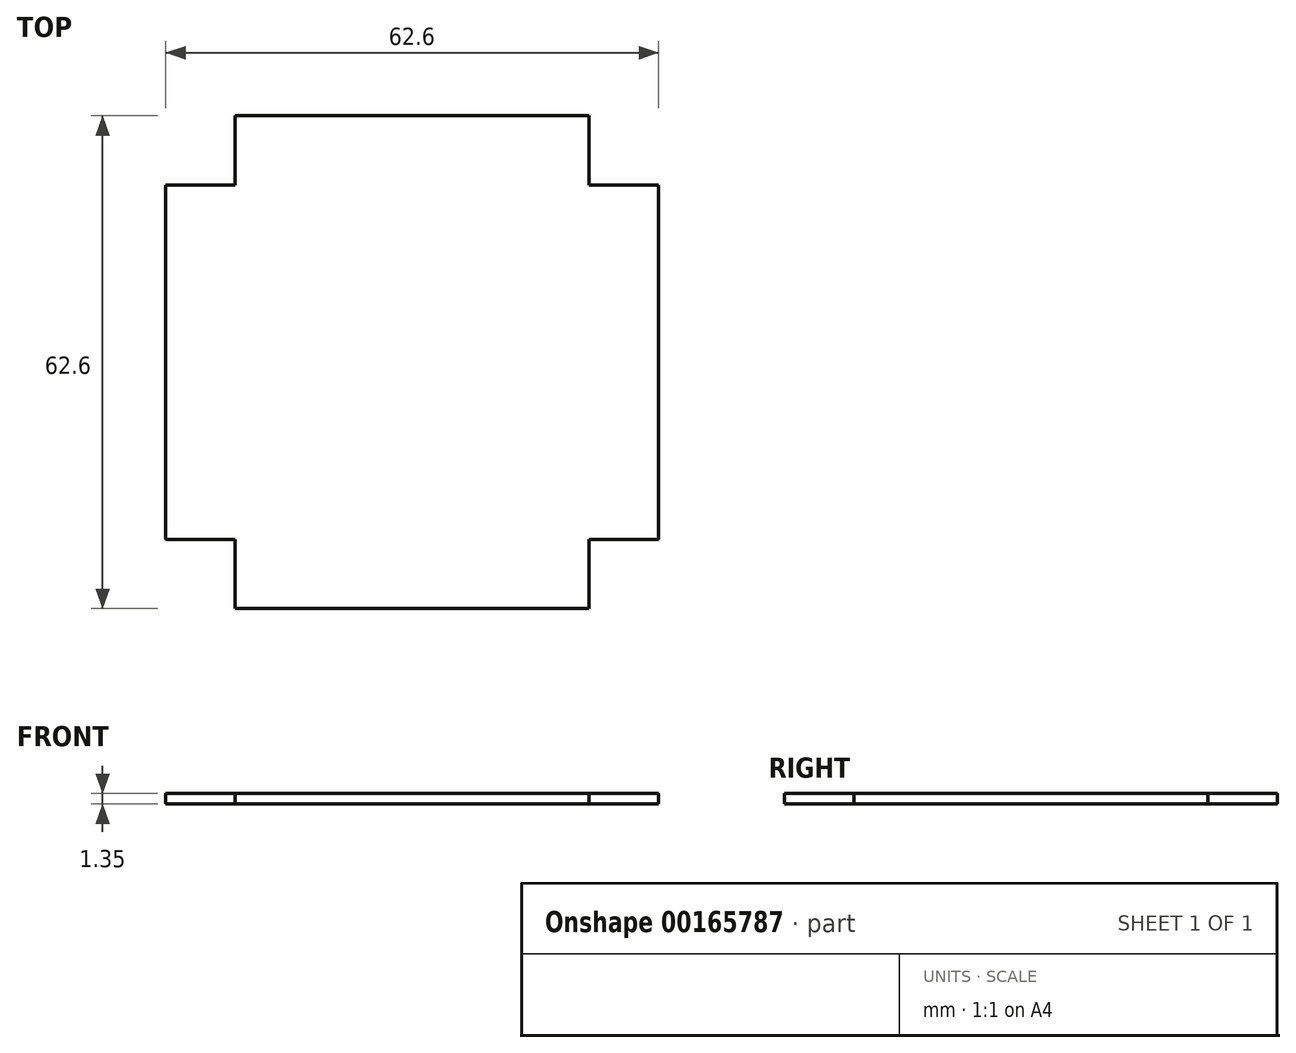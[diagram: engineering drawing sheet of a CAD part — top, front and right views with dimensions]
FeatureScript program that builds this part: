
annotation { "Feature Type Name" : "Feature", "Feature Type Description" : "" }
export const myFeature = defineFeature(function(context is Context, id is Id, definition is map)
    precondition{}
    {
        {
            var Q0;
            Q0=qCreatedBy(makeId("Top.planeOp"),FACE);
            var sketch = newSketch(context, id + "F0", { "sketchPlane" : qUnion([Q0])});
            skLineSegment(sketch, "E0.bottom", {"start": v(31.3, 22.5) * mm, "end": v(-31.3, 22.5) * mm});
            skLineSegment(sketch, "E0.top", {"start": v(31.3, -22.5) * mm, "end": v(-31.3, -22.5) * mm});
            skLineSegment(sketch, "E0.left", {"start": v(31.3, 22.5) * mm, "end": v(31.3, -22.5) * mm});
            skLineSegment(sketch, "E0.right", {"start": v(-31.3, 22.5) * mm, "end": v(-31.3, -22.5) * mm});
            skPoint(sketch, "E0.middle", {"position": v(0, 0) * mm});
            skLineSegment(sketch, "E1.bottom", {"start": v(22.5, 31.3) * mm, "end": v(-22.5, 31.3) * mm});
            skLineSegment(sketch, "E1.top", {"start": v(22.5, -31.3) * mm, "end": v(-22.5, -31.3) * mm});
            skLineSegment(sketch, "E1.left", {"start": v(22.5, 31.3) * mm, "end": v(22.5, -31.3) * mm});
            skLineSegment(sketch, "E1.right", {"start": v(-22.5, 31.3) * mm, "end": v(-22.5, -31.3) * mm});
            skSolve(sketch);
        }
        {
            var Q0;
            Q0 = qSketchRegion(id + "F0", true);
            extrude(context, id + "F1", {"entities" : qUnion([Q0]), "depth" : 1.35 * mm});
        }
    });
